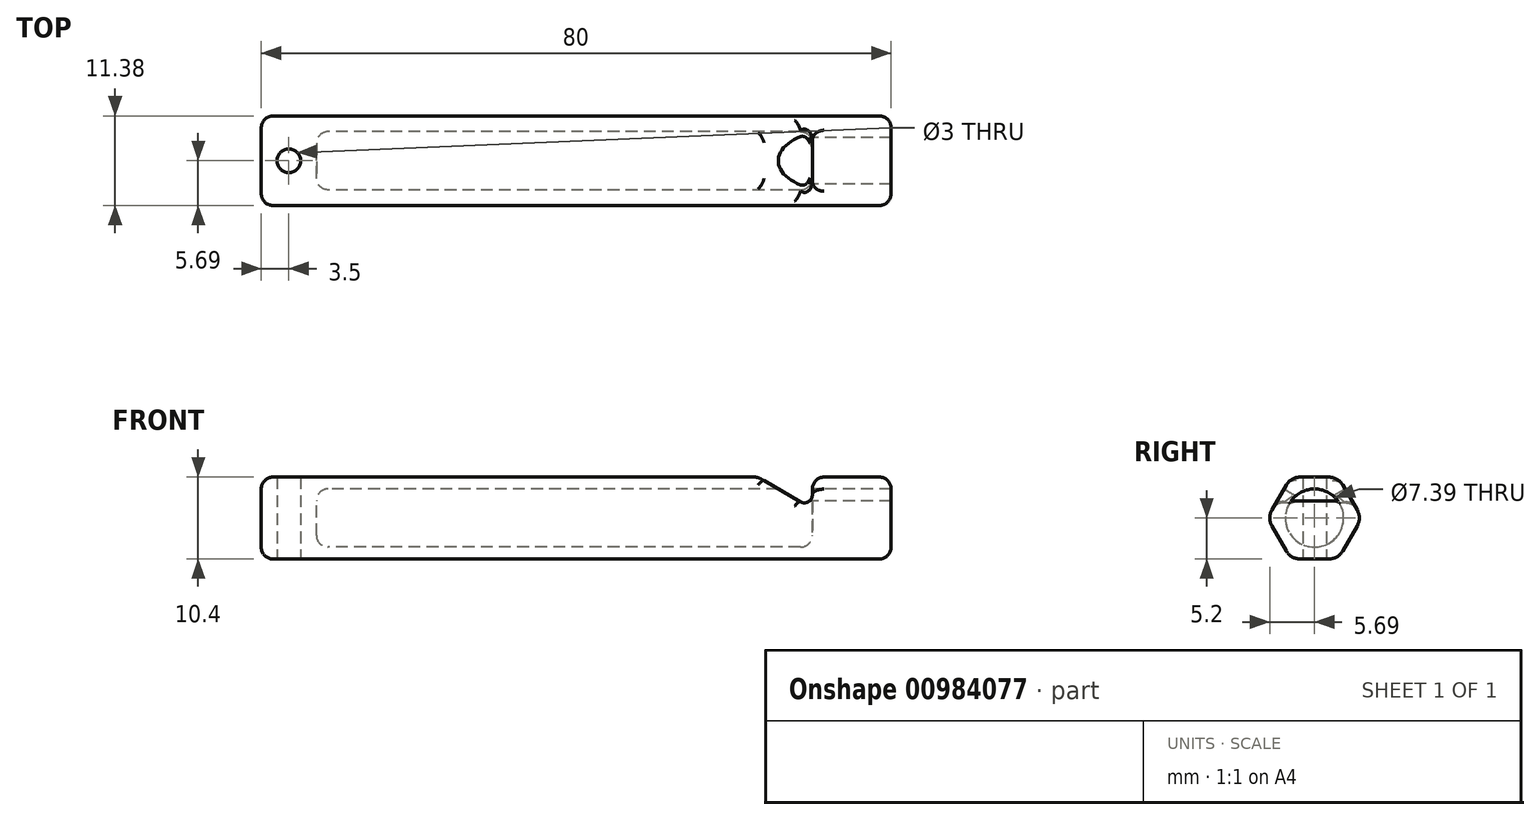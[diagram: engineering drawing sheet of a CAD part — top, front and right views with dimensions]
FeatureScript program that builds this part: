
annotation { "Feature Type Name" : "Feature", "Feature Type Description" : "" }
export const myFeature = defineFeature(function(context is Context, id is Id, definition is map)
    precondition{}
    {
        {
            var Q0;
            Q0=qCreatedBy(makeId("Right.planeOp"),FACE);
            var sketch = newSketch(context, id + "F0", { "sketchPlane" : qUnion([Q0])});
            skCircle(sketch, "E0.cCircle", {"center": v(0, 0) * mm, "radius": 5.2 * mm, "construction": true});
            skLineSegment(sketch, "E0.0", {"start": v(3, 5.2) * mm, "end": v(6, 0) * mm});
            skLineSegment(sketch, "E0.1", {"start": v(6, 0) * mm, "end": v(3, -5.2) * mm});
            skLineSegment(sketch, "E0.2", {"start": v(3, -5.2) * mm, "end": v(-3, -5.2) * mm});
            skLineSegment(sketch, "E0.3", {"start": v(-3, -5.2) * mm, "end": v(-6, 0) * mm});
            skLineSegment(sketch, "E0.4", {"start": v(-6, 0) * mm, "end": v(-3, 5.2) * mm});
            skLineSegment(sketch, "E0.5", {"start": v(-3, 5.2) * mm, "end": v(3, 5.2) * mm});
            skPoint(sketch, "E0.0.midPoint", {"position": v(4.5, 2.6) * mm});
            skCircle(sketch, "E1", {"center": v(0, 0) * mm, "radius": 3.7 * mm});
            skLineSegment(sketch, "E2", {"start": v(-2.97, 2.2) * mm, "end": v(2.97, 2.2) * mm});
            skSolve(sketch);
        }
        {
            var Q0;
            Q0=makeQuery(id+"F0.imprint","IMPRINT",FACE,{"disambiguationData":[TD([[makeQuery(id+"F0.imprint","IMPRINT",EDGE,{"derivedFrom":sQuery(id+"F0.wireOp",EDGE,"E0.0")}),-1.0]])]});
            var Q1;
            {var subQ0=sQuery(id+"F0.wireOp",EDGE,"E2");Q1=makeQuery(id+"F0.imprint","IMPRINT",FACE,{"disambiguationData":[TD([[makeQuery(id+"F0.imprint","IMPRINT",EDGE,{"derivedFrom":subQ0}),-1.0]])]});}
            var Q2;
            {var subQ0=sQuery(id+"F0.wireOp",EDGE,"E2");Q2=makeQuery(id+"F0.imprint","IMPRINT",FACE,{"disambiguationData":[TD([[makeQuery(id+"F0.imprint","IMPRINT",EDGE,{"derivedFrom":subQ0}),1.0]])]});}
            extrude(context, id + "F1", {"entities" : qUnion([Q0, Q1, Q2]), "oppositeDirection" : true, "depth" : 70 * mm, "offsetDistance" : 25 * mm});
        }
        {
            var Q0;
            Q0=makeQuery(id+"F0.imprint","IMPRINT",FACE,{"disambiguationData":[TD([[makeQuery(id+"F0.imprint","IMPRINT",EDGE,{"derivedFrom":sQuery(id+"F0.wireOp",EDGE,"E0.0")}),-1.0]])]});
            var Q1;
            {var subQ0=sQuery(id+"F0.wireOp",EDGE,"E2");Q1=makeQuery(id+"F0.imprint","IMPRINT",FACE,{"disambiguationData":[TD([[makeQuery(id+"F0.imprint","IMPRINT",EDGE,{"derivedFrom":subQ0}),-1.0]])]});}
            extrude(context, id + "F2", {"entities" : qUnion([Q0, Q1]), "operationType" : NewBodyOperationType.ADD, "depth" : 10 * mm, "offsetDistance" : 25 * mm});
        }
        {
            var Q0;
            {var subQ0=sQuery(id+"F0.wireOp",EDGE,"E2");Q0=makeQuery(id+"F0.imprint","IMPRINT",FACE,{"disambiguationData":[TD([[makeQuery(id+"F0.imprint","IMPRINT",EDGE,{"derivedFrom":subQ0}),1.0]])]});}
            var Q1;
            {var subQ0=sQuery(id+"F0.wireOp",EDGE,"E2");Q1=makeQuery(id+"F0.imprint","IMPRINT",FACE,{"disambiguationData":[TD([[makeQuery(id+"F0.imprint","IMPRINT",EDGE,{"derivedFrom":subQ0}),-1.0]])]});}
            var Q2;
            Q2=makeQuery(id+"F1.opExtrude","CAP_FACE",FACE,{"disambiguationData":[OSD([sQuery(id+"F0.wireOp",EDGE,"E0.0"),sQuery(id+"F0.wireOp",EDGE,"E0.1"),sQuery(id+"F0.wireOp",EDGE,"E0.2"),sQuery(id+"F0.wireOp",EDGE,"E0.3"),sQuery(id+"F0.wireOp",EDGE,"E0.4"),sQuery(id+"F0.wireOp",EDGE,"E0.5")])],"isStart":false});
            extrude(context, id + "F3", {"entities" : qUnion([Q0, Q1]), "operationType" : NewBodyOperationType.REMOVE, "endBound" : BoundingType.UP_TO_SURFACE, "oppositeDirection" : true, "depth" : 77 * mm, "endBoundEntityFace" : qUnion([Q2]), "hasOffset" : true, "offsetDistance" : 7 * mm});
        }
        {
            var Q0;
            Q0=qCreatedBy(makeId("Front.planeOp"),FACE);
            var sketch = newSketch(context, id + "F4", { "sketchPlane" : qUnion([Q0])});
            skLineSegment(sketch, "E3", {"start": v(-6.93, 5.2) * mm, "end": v(-1.5, 2.06) * mm});
            skLineSegment(sketch, "E4", {"start": v(0, 2.93) * mm, "end": v(0, 5.2) * mm});
            skLineSegment(sketch, "E5", {"start": v(0, 5.2) * mm, "end": v(-6.93, 5.2) * mm});
            skPoint(sketch, "E6.visualSharp", {"position": v(0, 1.2) * mm});
            skArc(sketch, "E6.filletArc", {"start": v(-1.5, 2.06) * mm, "mid": v(-0.5, 2.06) * mm, "end": v(0, 2.93) * mm});
            skSolve(sketch);
        }
        {
            var Q0;
            Q0 = qSketchRegion(id + "F4", true);
            extrude(context, id + "F5", {"entities" : qUnion([Q0]), "operationType" : NewBodyOperationType.REMOVE, "endBound" : BoundingType.SYMMETRIC, "oppositeDirection" : true, "depth" : 25 * mm, "offsetDistance" : 25 * mm});
        }
        {
            var Q0;
            {var subQ0=sQuery(id+"F0.wireOp",EDGE,"E0.4");var subQ1=sQuery(id+"F0.wireOp",EDGE,"E0.3");Q0=makeQuery(id+"F2.boolean.opBoolean","MERGE",EDGE,{"derivedFrom":[makeQuery(id+"F1.opExtrude","SWEPT_EDGE",EDGE,{"disambiguationData":[OSD([subQ1,subQ0])]}),makeQuery(id+"F2.opExtrude","SWEPT_EDGE",EDGE,{"disambiguationData":[OSD([subQ1,subQ0])]})]});}
            var Q1;
            {var subQ0=sQuery(id+"F0.wireOp",EDGE,"E0.4");var subQ1=sQuery(id+"F0.wireOp",EDGE,"E0.5");Q1=makeQuery(id+"F5.boolean.opBoolean","SPLIT",EDGE,{"disambiguationData":[TD([makeQuery(id+"F5.opExtrude","SWEPT_FACE",FACE,{"disambiguationData":[OSD([sQuery(id+"F4.wireOp",EDGE,"E3")])]})])],"derivedFrom":makeQuery(id+"F2.boolean.opBoolean","MERGE",EDGE,{"derivedFrom":[makeQuery(id+"F1.opExtrude","SWEPT_EDGE",EDGE,{"disambiguationData":[OSD([subQ0,subQ1])]}),makeQuery(id+"F2.opExtrude","SWEPT_EDGE",EDGE,{"disambiguationData":[OSD([subQ0,subQ1])]})]})});}
            var Q2;
            {var subQ0=sQuery(id+"F0.wireOp",EDGE,"E0.0");var subQ1=sQuery(id+"F0.wireOp",EDGE,"E0.5");Q2=makeQuery(id+"F5.boolean.opBoolean","SPLIT",EDGE,{"disambiguationData":[TD([makeQuery(id+"F5.opExtrude","SWEPT_FACE",FACE,{"disambiguationData":[OSD([sQuery(id+"F4.wireOp",EDGE,"E3")])]})])],"derivedFrom":makeQuery(id+"F2.boolean.opBoolean","MERGE",EDGE,{"derivedFrom":[makeQuery(id+"F1.opExtrude","SWEPT_EDGE",EDGE,{"disambiguationData":[OSD([subQ0,subQ1])]}),makeQuery(id+"F2.opExtrude","SWEPT_EDGE",EDGE,{"disambiguationData":[OSD([subQ0,subQ1])]})]})});}
            var Q3;
            {var subQ0=sQuery(id+"F0.wireOp",EDGE,"E0.1");var subQ1=sQuery(id+"F0.wireOp",EDGE,"E0.0");Q3=makeQuery(id+"F2.boolean.opBoolean","MERGE",EDGE,{"derivedFrom":[makeQuery(id+"F1.opExtrude","SWEPT_EDGE",EDGE,{"disambiguationData":[OSD([subQ1,subQ0])]}),makeQuery(id+"F2.opExtrude","SWEPT_EDGE",EDGE,{"disambiguationData":[OSD([subQ1,subQ0])]})]});}
            var Q4;
            {var subQ0=sQuery(id+"F0.wireOp",EDGE,"E0.2");var subQ1=sQuery(id+"F0.wireOp",EDGE,"E0.1");Q4=makeQuery(id+"F2.boolean.opBoolean","MERGE",EDGE,{"derivedFrom":[makeQuery(id+"F1.opExtrude","SWEPT_EDGE",EDGE,{"disambiguationData":[OSD([subQ1,subQ0])]}),makeQuery(id+"F2.opExtrude","SWEPT_EDGE",EDGE,{"disambiguationData":[OSD([subQ1,subQ0])]})]});}
            var Q5;
            {var subQ0=sQuery(id+"F0.wireOp",EDGE,"E0.3");var subQ1=sQuery(id+"F0.wireOp",EDGE,"E0.2");Q5=makeQuery(id+"F2.boolean.opBoolean","MERGE",EDGE,{"derivedFrom":[makeQuery(id+"F1.opExtrude","SWEPT_EDGE",EDGE,{"disambiguationData":[OSD([subQ1,subQ0])]}),makeQuery(id+"F2.opExtrude","SWEPT_EDGE",EDGE,{"disambiguationData":[OSD([subQ1,subQ0])]})]});}
            var Q6;
            {var subQ0=sQuery(id+"F0.wireOp",EDGE,"E1");var subQ1=sQuery(id+"F0.wireOp",EDGE,"E0.5");var subQ2=sQuery(id+"F0.wireOp",EDGE,"E0.4");Q6=makeQuery(id+"F5.boolean.opBoolean","SPLIT",EDGE,{"disambiguationData":[TD([makeQuery(id+"F3.boolean.opBoolean","COPY",FACE,{"derivedFrom":makeQuery(id+"F3.opExtrude","CAP_FACE",FACE,{"disambiguationData":[OSD([subQ0])],"isStart":true})})])],"derivedFrom":makeQuery(id+"F2.boolean.opBoolean","MERGE",EDGE,{"derivedFrom":[makeQuery(id+"F1.opExtrude","SWEPT_EDGE",EDGE,{"disambiguationData":[OSD([subQ2,subQ1])]}),makeQuery(id+"F2.opExtrude","SWEPT_EDGE",EDGE,{"disambiguationData":[OSD([subQ2,subQ1])]})]})});}
            var Q7;
            {var subQ0=sQuery(id+"F0.wireOp",EDGE,"E1");var subQ1=sQuery(id+"F0.wireOp",EDGE,"E0.5");var subQ2=sQuery(id+"F0.wireOp",EDGE,"E0.0");Q7=makeQuery(id+"F5.boolean.opBoolean","SPLIT",EDGE,{"disambiguationData":[TD([makeQuery(id+"F3.boolean.opBoolean","COPY",FACE,{"derivedFrom":makeQuery(id+"F3.opExtrude","CAP_FACE",FACE,{"disambiguationData":[OSD([subQ0])],"isStart":true})})])],"derivedFrom":makeQuery(id+"F2.boolean.opBoolean","MERGE",EDGE,{"derivedFrom":[makeQuery(id+"F1.opExtrude","SWEPT_EDGE",EDGE,{"disambiguationData":[OSD([subQ2,subQ1])]}),makeQuery(id+"F2.opExtrude","SWEPT_EDGE",EDGE,{"disambiguationData":[OSD([subQ2,subQ1])]})]})});}
            var Q8;
            {var subQ0=sQuery(id+"F0.wireOp",EDGE,"E0.5");var subQ1=sQuery(id+"F0.wireOp",EDGE,"E0.0");Q8=makeQuery(id+"F5.boolean.opBoolean","SPLIT",EDGE,{"disambiguationData":[TD([makeQuery(id+"F5.opExtrude","SWEPT_FACE",FACE,{"disambiguationData":[OSD([sQuery(id+"F4.wireOp",EDGE,"E4")])]})])],"derivedFrom":makeQuery(id+"F2.boolean.opBoolean","MERGE",EDGE,{"derivedFrom":[makeQuery(id+"F1.opExtrude","SWEPT_EDGE",EDGE,{"disambiguationData":[OSD([subQ1,subQ0])]}),makeQuery(id+"F2.opExtrude","SWEPT_EDGE",EDGE,{"disambiguationData":[OSD([subQ1,subQ0])]})]})});}
            var Q9;
            {var subQ0=sQuery(id+"F0.wireOp",EDGE,"E0.5");var subQ1=sQuery(id+"F0.wireOp",EDGE,"E0.4");Q9=makeQuery(id+"F5.boolean.opBoolean","SPLIT",EDGE,{"disambiguationData":[TD([makeQuery(id+"F5.opExtrude","SWEPT_FACE",FACE,{"disambiguationData":[OSD([sQuery(id+"F4.wireOp",EDGE,"E4")])]})])],"derivedFrom":makeQuery(id+"F2.boolean.opBoolean","MERGE",EDGE,{"derivedFrom":[makeQuery(id+"F1.opExtrude","SWEPT_EDGE",EDGE,{"disambiguationData":[OSD([subQ1,subQ0])]}),makeQuery(id+"F2.opExtrude","SWEPT_EDGE",EDGE,{"disambiguationData":[OSD([subQ1,subQ0])]})]})});}
            fillet(context, id + "F6", {"entities" : qUnion([Q0, Q1, Q2, Q3, Q4, Q5, Q6, Q7, Q8, Q9]), "radius" : 2 * mm, "tangentPropagation" : true, "allowEdgeOverflow" : false});
        }
        {
            var Q0;
            Q0=qCreatedBy(makeId("Top.planeOp"),FACE);
            var sketch = newSketch(context, id + "F7", { "sketchPlane" : qUnion([Q0])});
            skCircle(sketch, "E7", {"center": v(-66.5, 0) * mm, "radius": 1.5 * mm});
            skSolve(sketch);
        }
        {
            var Q0;
            Q0 = qSketchRegion(id + "F7", true);
            extrude(context, id + "F8", {"entities" : qUnion([Q0]), "operationType" : NewBodyOperationType.REMOVE, "endBound" : BoundingType.SYMMETRIC, "depth" : 25 * mm, "offsetDistance" : 25 * mm});
        }
        {
            var Q0;
            Q0=makeQuery(id+"F2.opExtrude","CAP_EDGE",EDGE,{"disambiguationData":[OSD([sQuery(id+"F0.wireOp",EDGE,"E0.2")])],"isStart":false});
            var Q1;
            {var subQ0=sQuery(id+"F0.wireOp",EDGE,"E0.4");Q1=makeQuery(id+"F5.boolean.opBoolean","INTERSECT",EDGE,{"derivedFrom":[makeQuery(id+"F2.boolean.opBoolean","MERGE",FACE,{"derivedFrom":[makeQuery(id+"F1.opExtrude","SWEPT_FACE",FACE,{"disambiguationData":[OSD([subQ0])]}),makeQuery(id+"F2.opExtrude","SWEPT_FACE",FACE,{"disambiguationData":[OSD([subQ0])]})]}),makeQuery(id+"F5.opExtrude","SWEPT_FACE",FACE,{"disambiguationData":[OSD([sQuery(id+"F4.wireOp",EDGE,"E3")])]})]});}
            var Q2;
            Q2=makeQuery(id+"F1.opExtrude","CAP_EDGE",EDGE,{"disambiguationData":[OSD([sQuery(id+"F0.wireOp",EDGE,"E0.1")])],"isStart":false});
            var Q3;
            Q3=makeQuery(id+"F3.boolean.opBoolean","COPY",EDGE,{"derivedFrom":makeQuery(id+"F3.opExtrude","CAP_EDGE",EDGE,{"disambiguationData":[OSD([sQuery(id+"F0.wireOp",EDGE,"E1")])],"isStart":true})});
            var Q4;
            Q4=makeQuery(id+"F3.boolean.opBoolean","COPY",EDGE,{"derivedFrom":makeQuery(id+"F3.opExtrude","CAP_EDGE",EDGE,{"disambiguationData":[OSD([sQuery(id+"F0.wireOp",EDGE,"E1")])],"isStart":false})});
            fillet(context, id + "F9", {"entities" : qUnion([Q0, Q1, Q2, Q3, Q4]), "radius" : 1.5 * mm, "tangentPropagation" : true, "allowEdgeOverflow" : false});
        }
        {
            var Q0;
            Q0=makeQuery(id+"F1.opExtrude","CAP_FACE",FACE,{"disambiguationData":[OSD([sQuery(id+"F0.wireOp",EDGE,"E0.0"),sQuery(id+"F0.wireOp",EDGE,"E0.1"),sQuery(id+"F0.wireOp",EDGE,"E0.2"),sQuery(id+"F0.wireOp",EDGE,"E0.3"),sQuery(id+"F0.wireOp",EDGE,"E0.4"),sQuery(id+"F0.wireOp",EDGE,"E0.5")])],"isStart":false});
            cPlane(context, id + "F10", {"entities" : qUnion([Q0]), "cplaneType" : CPlaneType.OFFSET, "offset" : 5 * mm, "width" : 150 * mm, "height" : 150 * mm});
        }
        {
            var Q0;
            Q0=sQuery(id+"F0.wireOp",VERTEX,"E0.cCircle.center");
            var Q1;
            Q1=qCreatedBy(makeId("Top.planeOp"),FACE);
            cPlane(context, id + "F12", {"entities" : qUnion([Q0, Q1]), "cplaneType" : CPlaneType.PLANE_POINT, "offset" : 25 * mm, "width" : 150 * mm, "height" : 150 * mm});
        }
    });
